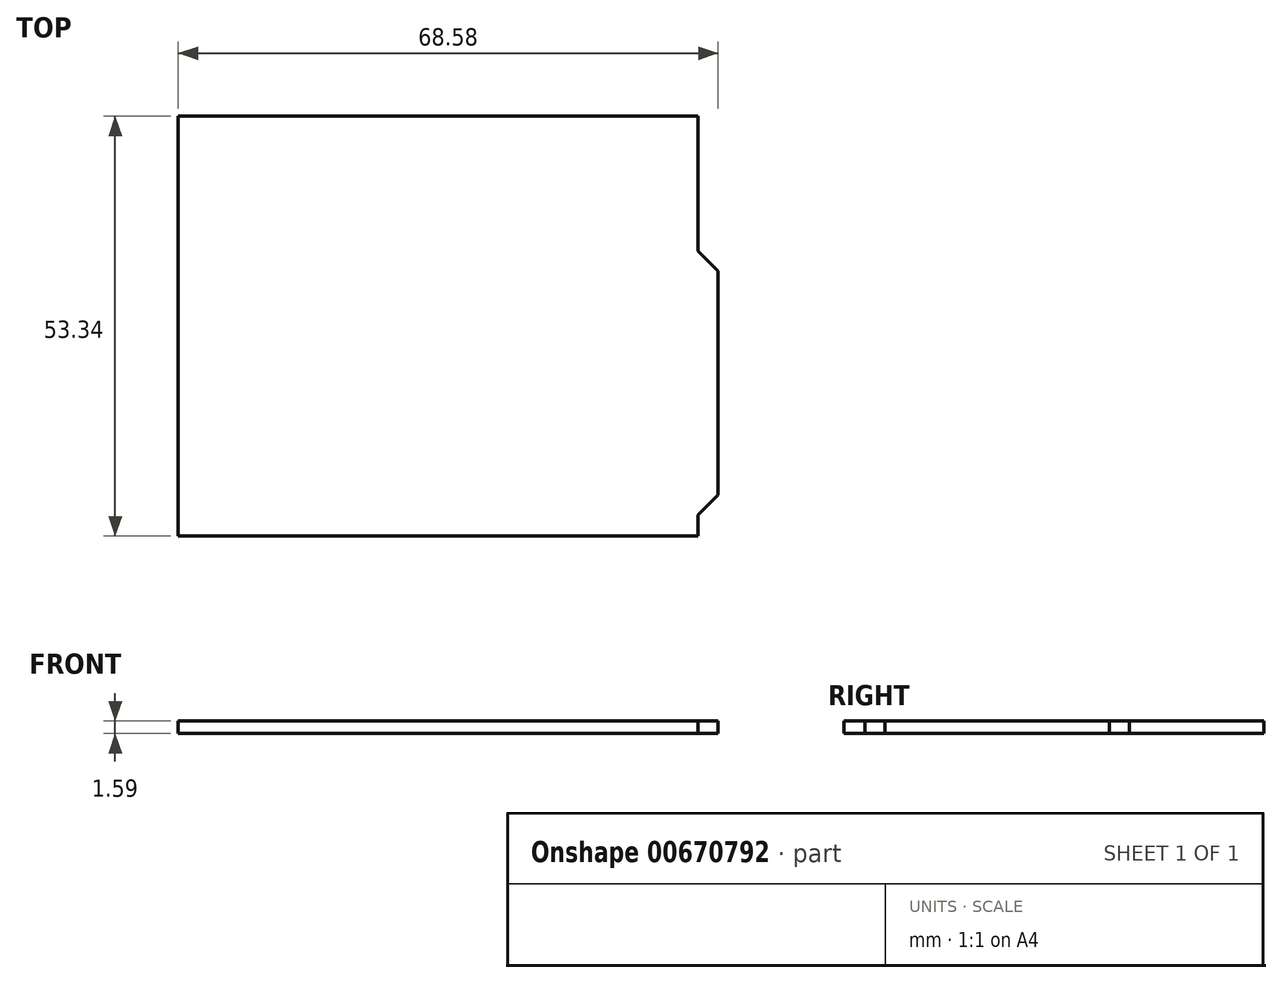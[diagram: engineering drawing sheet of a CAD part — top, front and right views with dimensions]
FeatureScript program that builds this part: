
annotation { "Feature Type Name" : "Feature", "Feature Type Description" : "" }
export const myFeature = defineFeature(function(context is Context, id is Id, definition is map)
    precondition{}
    {
        {
            var Q0;
            Q0=qCreatedBy(makeId("Top.planeOp"),FACE);
            var sketch = newSketch(context, id + "F0", { "sketchPlane" : qUnion([Q0])});
            skLineSegment(sketch, "E0", {"start": v(-33.02, 26.67) * mm, "end": v(33.02, 26.67) * mm});
            skLineSegment(sketch, "E1", {"start": v(33.02, 26.67) * mm, "end": v(33.02, -26.67) * mm});
            skLineSegment(sketch, "E2", {"start": v(33.02, -26.67) * mm, "end": v(-33.02, -26.67) * mm});
            skLineSegment(sketch, "E3", {"start": v(-33.02, 26.67) * mm, "end": v(-33.02, -26.67) * mm});
            skLineSegment(sketch, "E4", {"start": v(0, 0) * mm, "end": v(-33.02, 0) * mm, "construction": true});
            skLineSegment(sketch, "E5", {"start": v(0, 0) * mm, "end": v(0, 26.67) * mm, "construction": true});
            skLineSegment(sketch, "E6", {"start": v(33.02, 9.57) * mm, "end": v(35.56, 7.03) * mm});
            skLineSegment(sketch, "E7", {"start": v(33.02, -24) * mm, "end": v(35.56, -21.46) * mm});
            skLineSegment(sketch, "E8", {"start": v(35.56, 7.03) * mm, "end": v(35.56, -21.46) * mm});
            skSolve(sketch);
        }
        {
            var Q0;
            Q0 = qSketchRegion(id + "F0", true);
            extrude(context, id + "F1", {"entities" : qUnion([Q0]), "depth" : 1.59 * mm, "offsetDistance" : 25 * mm});
        }
    });
